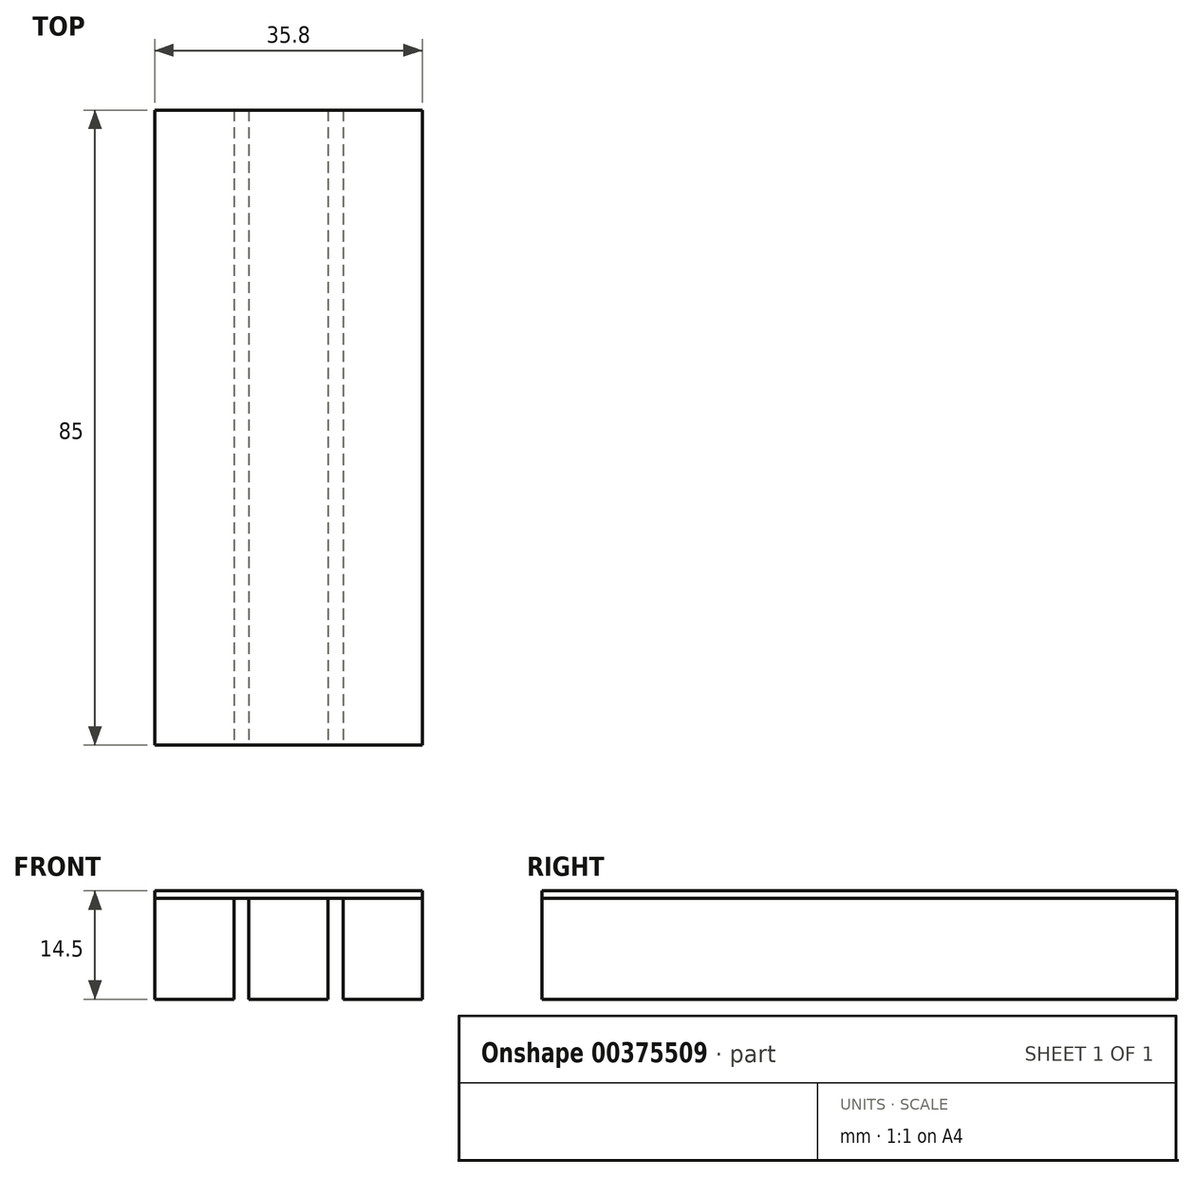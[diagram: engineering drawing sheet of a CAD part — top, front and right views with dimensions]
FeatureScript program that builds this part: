
annotation { "Feature Type Name" : "Feature", "Feature Type Description" : "" }
export const myFeature = defineFeature(function(context is Context, id is Id, definition is map)
    precondition{}
    {
        {
            var Q0;
            Q0=qCreatedBy(makeId("Top.planeOp"),FACE);
            var sketch = newSketch(context, id + "F0", { "sketchPlane" : qUnion([Q0])});
            skLineSegment(sketch, "E0.bottom", {"start": v(5.3, 42.5) * mm, "end": v(-5.3, 42.5) * mm});
            skLineSegment(sketch, "E0.top", {"start": v(5.3, -42.5) * mm, "end": v(-5.3, -42.5) * mm});
            skLineSegment(sketch, "E0.left", {"start": v(5.3, 42.5) * mm, "end": v(5.3, -42.5) * mm});
            skLineSegment(sketch, "E0.right", {"start": v(-5.3, 42.5) * mm, "end": v(-5.3, -42.5) * mm});
            skPoint(sketch, "E0.middle", {"position": v(0, 0) * mm});
            skLineSegment(sketch, "E1.1.0.0", {"start": v(17.9, -42.5) * mm, "end": v(7.3, -42.5) * mm});
            skLineSegment(sketch, "E1.1.0.1", {"start": v(17.9, 42.5) * mm, "end": v(17.9, -42.5) * mm});
            skLineSegment(sketch, "E1.1.0.2", {"start": v(7.3, 42.5) * mm, "end": v(7.3, -42.5) * mm});
            skPoint(sketch, "E1.1.0.3", {"position": v(12.6, 0) * mm});
            skLineSegment(sketch, "E1.1.0.4", {"start": v(17.9, 42.5) * mm, "end": v(7.3, 42.5) * mm});
            skLineSegment(sketch, "E1.2.0.0", {"start": v(30.5, -42.5) * mm, "end": v(19.9, -42.5) * mm});
            skLineSegment(sketch, "E1.2.0.1", {"start": v(30.5, 42.5) * mm, "end": v(30.5, -42.5) * mm});
            skLineSegment(sketch, "E1.2.0.2", {"start": v(19.9, 42.5) * mm, "end": v(19.9, -42.5) * mm});
            skPoint(sketch, "E1.2.0.3", {"position": v(25.2, 0) * mm});
            skLineSegment(sketch, "E1.2.0.4", {"start": v(30.5, 42.5) * mm, "end": v(19.9, 42.5) * mm});
            skLineSegment(sketch, "E1.direction1", {"start": v(-5.3, -42.5) * mm, "end": v(7.3, -42.5) * mm, "construction": true});
            skSolve(sketch);
        }
        {
            var Q0;
            Q0 = qSketchRegion(id + "F0", true);
            extrude(context, id + "F1", {"entities" : qUnion([Q0]), "depth" : 13.5 * mm});
        }
        {
            var Q0;
            Q0=makeQuery(id+"F1.opExtrude","CAP_FACE",FACE,{"disambiguationData":[OSD([sQuery(id+"F0.wireOp",EDGE,"E0.bottom"),sQuery(id+"F0.wireOp",EDGE,"E0.top"),sQuery(id+"F0.wireOp",EDGE,"E0.left"),sQuery(id+"F0.wireOp",EDGE,"E0.right")])],"isStart":false});
            var sketch = newSketch(context, id + "F2", { "sketchPlane" : qUnion([Q0])});
            skLineSegment(sketch, "E2.bottom", {"start": v(-5.3, 42.5) * mm, "end": v(30.5, 42.5) * mm});
            skLineSegment(sketch, "E2.top", {"start": v(-5.3, -42.5) * mm, "end": v(30.5, -42.5) * mm});
            skLineSegment(sketch, "E2.left", {"start": v(-5.3, 42.5) * mm, "end": v(-5.3, -42.5) * mm});
            skLineSegment(sketch, "E2.right", {"start": v(30.5, 42.5) * mm, "end": v(30.5, -42.5) * mm});
            skSolve(sketch);
        }
        {
            var Q0;
            Q0 = qSketchRegion(id + "F2", true);
            extrude(context, id + "F3", {"entities" : qUnion([Q0]), "depth" : 1 * mm});
        }
    });
